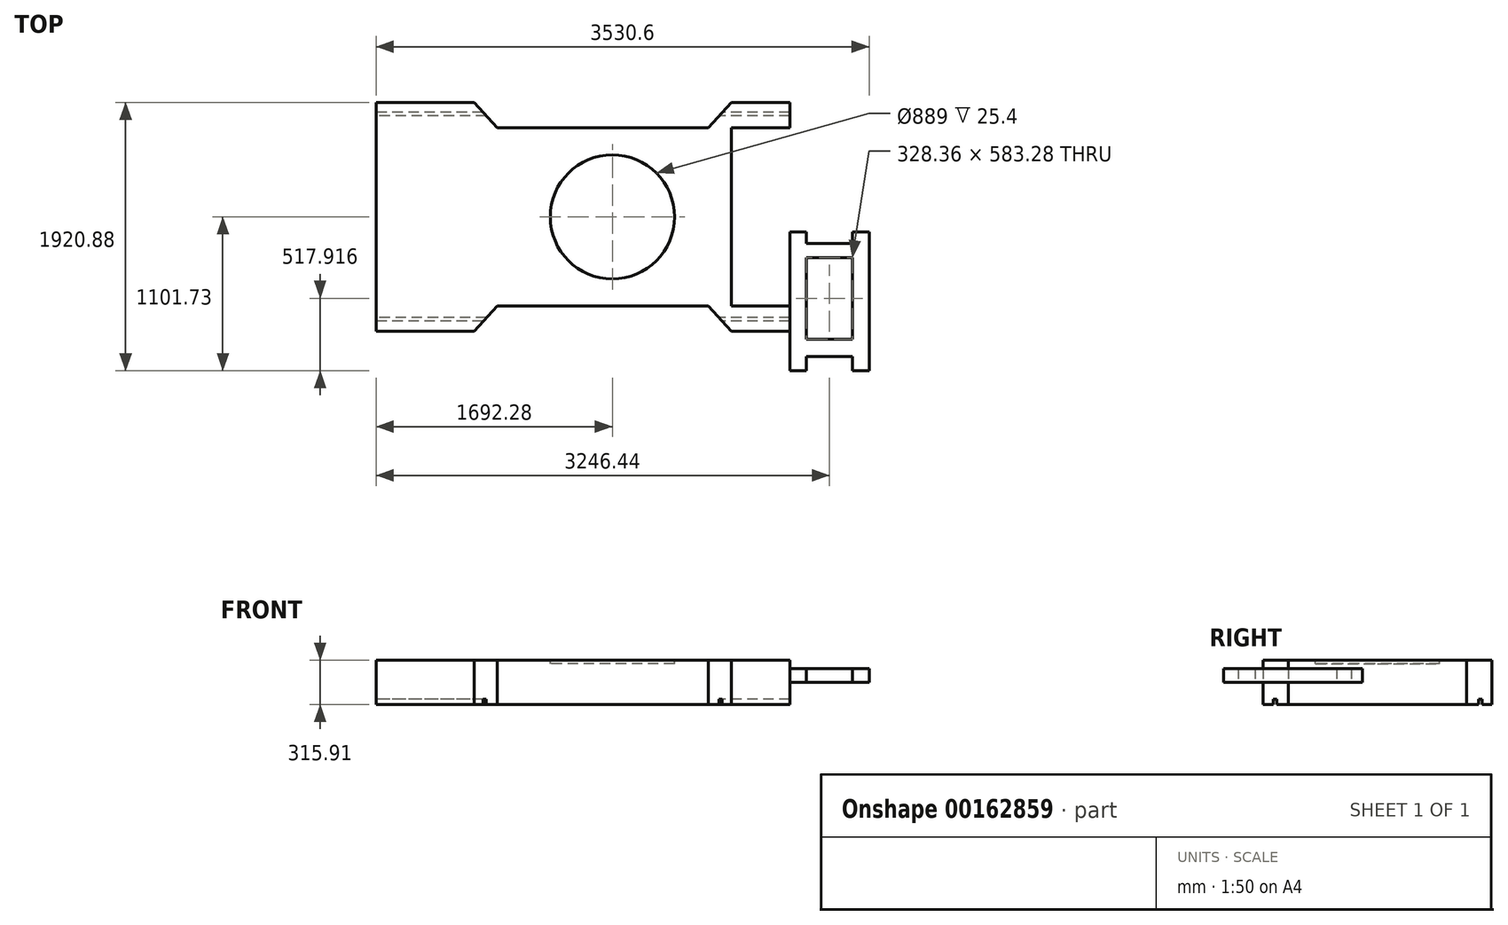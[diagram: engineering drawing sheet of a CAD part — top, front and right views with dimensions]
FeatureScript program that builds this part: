
annotation { "Feature Type Name" : "Feature", "Feature Type Description" : "" }
export const myFeature = defineFeature(function(context is Context, id is Id, definition is map)
    precondition{}
    {
        {
            var Q0;
            Q0=qCreatedBy(makeId("Top.planeOp"),FACE);
            var sketch = newSketch(context, id + "F0", { "sketchPlane" : qUnion([Q0])});
            skLineSegment(sketch, "E0.bottom", {"start": v(350.84, -819.15) * mm, "end": v(-350.84, -819.15) * mm});
            skLineSegment(sketch, "E0.top", {"start": v(350.84, 819.15) * mm, "end": v(-350.84, 819.15) * mm});
            skLineSegment(sketch, "E0.left", {"start": v(350.84, -819.15) * mm, "end": v(350.84, 819.15) * mm});
            skLineSegment(sketch, "E0.right", {"start": v(-350.84, -819.15) * mm, "end": v(-350.84, 819.15) * mm});
            skPoint(sketch, "E0.middle", {"position": v(0, 0) * mm});
            skLineSegment(sketch, "E1.bottom", {"start": v(350.84, -638.18) * mm, "end": v(2611.44, -638.17) * mm});
            skLineSegment(sketch, "E1.top", {"start": v(350.84, 638.17) * mm, "end": v(2611.44, 638.18) * mm});
            skPoint(sketch, "E1.middle", {"position": v(1538.92, 0) * mm});
            skPoint(sketch, "E1.left.end.orphan", {"position": v(-253.76, 638.17) * mm});
            skPoint(sketch, "E2.orphan", {"position": v(-253.76, -638.18) * mm});
            skLineSegment(sketch, "E3", {"start": v(350.84, -819.15) * mm, "end": v(515.94, -638.18) * mm});
            skLineSegment(sketch, "E4.MirrorCS", {"start": v(350.84, 819.15) * mm, "end": v(515.94, 638.18) * mm});
            skLineSegment(sketch, "E5", {"start": v(2027.24, 638.17) * mm, "end": v(2027.24, -638.17) * mm});
            skLineSegment(sketch, "E6", {"start": v(2192.34, 819.15) * mm, "end": v(2192.34, -732.4) * mm});
            skLineSegment(sketch, "E7", {"start": v(2192.34, -819.15) * mm, "end": v(2027.24, -638.17) * mm});
            skLineSegment(sketch, "E8", {"start": v(2192.34, -819.15) * mm, "end": v(2192.34, -732.4) * mm});
            skLineSegment(sketch, "E9", {"start": v(2027.24, 638.17) * mm, "end": v(2192.34, 819.15) * mm});
            skLineSegment(sketch, "E10", {"start": v(2611.44, 819.15) * mm, "end": v(2611.44, -1032) * mm});
            skLineSegment(sketch, "E11", {"start": v(2192.34, -819.15) * mm, "end": v(2611.44, -819.15) * mm});
            skLineSegment(sketch, "E12", {"start": v(2192.34, 819.15) * mm, "end": v(2611.44, 819.15) * mm});
            skPoint(sketch, "E13.orphan", {"position": v(3331.6, 638.18) * mm});
            skPoint(sketch, "E14.orphan", {"position": v(3331.6, -638.17) * mm});
            skLineSegment(sketch, "E15.bottom", {"start": v(2611.44, -107.95) * mm, "end": v(3179.76, -107.95) * mm});
            skLineSegment(sketch, "E15.top", {"start": v(2611.44, -1101.73) * mm, "end": v(3179.76, -1101.73) * mm});
            skLineSegment(sketch, "E15.left", {"start": v(2611.44, -107.95) * mm, "end": v(2611.44, -1101.73) * mm});
            skLineSegment(sketch, "E15.right", {"start": v(3179.76, -107.95) * mm, "end": v(3179.76, -1101.73) * mm});
            skLineSegment(sketch, "E16.bottom", {"start": v(3059.78, -875.45) * mm, "end": v(2731.42, -875.45) * mm});
            skLineSegment(sketch, "E16.top", {"start": v(3059.78, -292.18) * mm, "end": v(2731.42, -292.18) * mm});
            skLineSegment(sketch, "E16.left", {"start": v(3059.78, -875.45) * mm, "end": v(3059.78, -292.18) * mm});
            skLineSegment(sketch, "E16.right", {"start": v(2731.42, -875.45) * mm, "end": v(2731.42, -292.18) * mm});
            skPoint(sketch, "E16.middle", {"position": v(2895.6, -583.81) * mm});
            skPoint(sketch, "E16.middle.positionSnap0", {"position": v(2895.6, -1101.73) * mm});
            skPoint(sketch, "E16.centerSnap0", {"position": v(2895.6, -1101.73) * mm});
            skLineSegment(sketch, "E17.bottom", {"start": v(3059.78, -1204.11) * mm, "end": v(2731.42, -1204.11) * mm});
            skLineSegment(sketch, "E17.top", {"start": v(3059.78, -999.34) * mm, "end": v(2731.42, -999.34) * mm});
            skLineSegment(sketch, "E17.left", {"start": v(3059.78, -1204.11) * mm, "end": v(3059.78, -999.34) * mm});
            skLineSegment(sketch, "E17.right", {"start": v(2731.42, -1204.11) * mm, "end": v(2731.42, -999.34) * mm});
            skLineSegment(sketch, "E18.bottom", {"start": v(3059.78, -189.27) * mm, "end": v(2731.42, -189.27) * mm});
            skLineSegment(sketch, "E18.top", {"start": v(3059.78, -26.63) * mm, "end": v(2731.42, -26.63) * mm});
            skLineSegment(sketch, "E18.left", {"start": v(3059.78, -189.27) * mm, "end": v(3059.78, -26.63) * mm});
            skLineSegment(sketch, "E18.right", {"start": v(2731.42, -189.27) * mm, "end": v(2731.42, -26.63) * mm});
            skPoint(sketch, "E18.middle", {"position": v(2895.6, -107.95) * mm});
            skSolve(sketch);
        }
        {
            var Q0;
            {var subQ0=sQuery(id+"F0.wireOp",EDGE,"E4.MirrorCS");Q0=makeQuery(id+"F0.imprint","IMPRINT",FACE,{"disambiguationData":[TD([[makeQuery(id+"F0.imprint","IMPRINT",EDGE,{"derivedFrom":subQ0}),-1.0]])]});}
            var Q1;
            {var subQ0=sQuery(id+"F0.wireOp",EDGE,"E3");Q1=makeQuery(id+"F0.imprint","IMPRINT",FACE,{"disambiguationData":[TD([[makeQuery(id+"F0.imprint","IMPRINT",EDGE,{"derivedFrom":subQ0}),1.0]])]});}
            var Q2;
            {var subQ7=sQuery(id+"F0.wireOp",EDGE,"E5");Q2=makeQuery(id+"F0.imprint","IMPRINT",FACE,{"disambiguationData":[TD([[makeQuery(id+"F0.imprint","IMPRINT",EDGE,{"derivedFrom":subQ7}),-1.0]])]});}
            var Q3;
            {var subQ0=sQuery(id+"F0.wireOp",EDGE,"E5");Q3=makeQuery(id+"F0.imprint","IMPRINT",FACE,{"disambiguationData":[TD([[makeQuery(id+"F0.imprint","IMPRINT",EDGE,{"derivedFrom":subQ0}),1.0]])]});}
            var Q4;
            {var subQ5=sQuery(id+"F0.wireOp",EDGE,"E12");Q4=makeQuery(id+"F0.imprint","IMPRINT",FACE,{"disambiguationData":[TD([[makeQuery(id+"F0.imprint","IMPRINT",EDGE,{"derivedFrom":subQ5}),-1.0]])]});}
            var Q5;
            {var subQ1=sQuery(id+"F0.wireOp",EDGE,"E1.bottom");var subQ7=sQuery(id+"F0.wireOp",EDGE,"E15.left");var subQ9=makeQuery(id+"F0.imprint","INTERSECT",VERTEX,{"derivedFrom":[subQ1,subQ7]});Q5=makeQuery(id+"F0.imprint","IMPRINT",FACE,{"disambiguationData":[TD([[makeQuery(id+"F0.imprint","IMPRINT",EDGE,{"disambiguationData":[TD([[subQ9,1.0]])],"derivedFrom":subQ1}),1.0]])]});}
            var Q6;
            {var subQ0=sQuery(id+"F0.wireOp",EDGE,"E8");Q6=makeQuery(id+"F0.imprint","IMPRINT",FACE,{"disambiguationData":[TD([[makeQuery(id+"F0.imprint","IMPRINT",EDGE,{"derivedFrom":subQ0}),-1.0]])]});}
            var Q7;
            {var subQ0=sQuery(id+"F0.wireOp",EDGE,"E7");Q7=makeQuery(id+"F0.imprint","IMPRINT",FACE,{"disambiguationData":[TD([[makeQuery(id+"F0.imprint","IMPRINT",EDGE,{"derivedFrom":subQ0}),-1.0]])]});}
            var Q8;
            {var subQ3=sQuery(id+"F0.wireOp",EDGE,"E0.bottom");Q8=makeQuery(id+"F0.imprint","IMPRINT",FACE,{"disambiguationData":[TD([[makeQuery(id+"F0.imprint","IMPRINT",EDGE,{"derivedFrom":subQ3}),-1.0]])]});}
            var Q9;
            {var subQ0=sQuery(id+"F0.wireOp",EDGE,"E9");Q9=makeQuery(id+"F0.imprint","IMPRINT",FACE,{"disambiguationData":[TD([[makeQuery(id+"F0.imprint","IMPRINT",EDGE,{"derivedFrom":subQ0}),-1.0]])]});}
            var Q10;
            {var subQ5=sQuery(id+"F0.wireOp",EDGE,"E15.right");Q10=makeQuery(id+"F0.imprint","IMPRINT",FACE,{"disambiguationData":[TD([[makeQuery(id+"F0.imprint","IMPRINT",EDGE,{"derivedFrom":subQ5}),-1.0]])]});}
            extrude(context, id + "F1", {"entities" : qUnion([Q0, Q1, Q2, Q3, Q4, Q5, Q6, Q7, Q8, Q9, Q10]), "depth" : 315.91 * mm});
        }
        {
            var Q0;
            {var subQ5=sQuery(id+"F0.wireOp",EDGE,"E15.right");Q0=makeQuery(id+"F0.imprint","IMPRINT",FACE,{"disambiguationData":[TD([[makeQuery(id+"F0.imprint","IMPRINT",EDGE,{"derivedFrom":subQ5}),-1.0]])]});}
            cPlane(context, id + "F2", {"entities" : qUnion([Q0]), "cplaneType" : CPlaneType.OFFSET, "offset" : 101.6 * mm, "width" : 152.4 * mm, "height" : 152.4 * mm});
        }
        {
            var Q0;
            Q0=makeQuery(id+"F1.opExtrude","SWEPT_FACE",FACE,{"disambiguationData":[OSD([sQuery(id+"F0.wireOp",EDGE,"E15.right")])]});
            var sketch = newSketch(context, id + "F3", { "sketchPlane" : qUnion([Q0])});
            skLineSegment(sketch, "E19.bottom", {"start": v(-1101.73, 315.91) * mm, "end": v(-107.95, 315.91) * mm});
            skLineSegment(sketch, "E19.top", {"start": v(-1101.73, 258.28) * mm, "end": v(-107.95, 258.28) * mm});
            skLineSegment(sketch, "E19.left", {"start": v(-1101.73, 315.91) * mm, "end": v(-1101.73, 258.28) * mm});
            skLineSegment(sketch, "E19.right", {"start": v(-107.95, 315.91) * mm, "end": v(-107.95, 258.28) * mm});
            skLineSegment(sketch, "E20.bottom", {"start": v(-1101.73, 0) * mm, "end": v(-107.95, 0) * mm});
            skLineSegment(sketch, "E20.top", {"start": v(-1101.73, 157.96) * mm, "end": v(-107.95, 157.96) * mm});
            skLineSegment(sketch, "E20.left", {"start": v(-1101.73, 0) * mm, "end": v(-1101.73, 157.96) * mm});
            skLineSegment(sketch, "E20.right", {"start": v(-107.95, 0) * mm, "end": v(-107.95, 157.96) * mm});
            skSolve(sketch);
        }
        {
            var Q0;
            Q0 = qSketchRegion(id + "F3", true);
            extrude(context, id + "F4", {"entities" : qUnion([Q0]), "operationType" : NewBodyOperationType.REMOVE, "oppositeDirection" : true, "depth" : 568.32 * mm});
        }
        {
            var Q0;
            Q0=makeQuery(id+"F1.opExtrude","CAP_FACE",FACE,{"disambiguationData":[OSD([sQuery(id+"F0.wireOp",EDGE,"E0.bottom"),sQuery(id+"F0.wireOp",EDGE,"E0.top"),sQuery(id+"F0.wireOp",EDGE,"E0.right"),sQuery(id+"F0.wireOp",EDGE,"E1.bottom"),sQuery(id+"F0.wireOp",EDGE,"E1.top"),sQuery(id+"F0.wireOp",EDGE,"E3"),sQuery(id+"F0.wireOp",EDGE,"E4.MirrorCS"),sQuery(id+"F0.wireOp",EDGE,"E7"),sQuery(id+"F0.wireOp",EDGE,"E9"),sQuery(id+"F0.wireOp",EDGE,"E10"),sQuery(id+"F0.wireOp",EDGE,"E11"),sQuery(id+"F0.wireOp",EDGE,"E12"),sQuery(id+"F0.wireOp",EDGE,"E15.bottom"),sQuery(id+"F0.wireOp",EDGE,"E15.top"),sQuery(id+"F0.wireOp",EDGE,"E15.left"),sQuery(id+"F0.wireOp",EDGE,"E15.right"),sQuery(id+"F0.wireOp",EDGE,"E16.bottom"),sQuery(id+"F0.wireOp",EDGE,"E16.top"),sQuery(id+"F0.wireOp",EDGE,"E16.left"),sQuery(id+"F0.wireOp",EDGE,"E16.right"),sQuery(id+"F0.wireOp",EDGE,"E17.top"),sQuery(id+"F0.wireOp",EDGE,"E17.left"),sQuery(id+"F0.wireOp",EDGE,"E17.right"),sQuery(id+"F0.wireOp",EDGE,"E18.bottom"),sQuery(id+"F0.wireOp",EDGE,"E18.left"),sQuery(id+"F0.wireOp",EDGE,"E18.right")])],"isStart":false});
            var sketch = newSketch(context, id + "F5", { "sketchPlane" : qUnion([Q0])});
            skCircle(sketch, "E21", {"center": v(1341.44, 0) * mm, "radius": 444.5 * mm});
            skPoint(sketch, "E21.centerSnap0", {"position": v(2611.44, 0) * mm});
            skSolve(sketch);
        }
        {
            var Q0;
            Q0=makeQuery(id+"F5.imprint","IMPRINT",FACE,{"disambiguationData":[TD([[makeQuery(id+"F5.imprint","IMPRINT",EDGE,{"derivedFrom":sQuery(id+"F5.wireOp",EDGE,"E21")}),1.0]])]});
            extrude(context, id + "F6", {"entities" : qUnion([Q0]), "operationType" : NewBodyOperationType.REMOVE, "oppositeDirection" : true, "depth" : 25.4 * mm});
        }
        {
            var Q0;
            Q0=makeQuery(id+"F1.opExtrude","SWEPT_FACE",FACE,{"disambiguationData":[OSD([sQuery(id+"F0.wireOp",EDGE,"E0.right")])]});
            var sketch = newSketch(context, id + "F7", { "sketchPlane" : qUnion([Q0])});
            skLineSegment(sketch, "E22.bottom", {"start": v(-722.31, -38.1) * mm, "end": v(-747.71, -38.1) * mm});
            skLineSegment(sketch, "E22.top", {"start": v(-722.31, 38.1) * mm, "end": v(-747.71, 38.1) * mm});
            skLineSegment(sketch, "E22.left", {"start": v(-722.31, -38.1) * mm, "end": v(-722.31, 38.1) * mm});
            skLineSegment(sketch, "E22.right", {"start": v(-747.71, -38.1) * mm, "end": v(-747.71, 38.1) * mm});
            skPoint(sketch, "E22.middle", {"position": v(-735.01, 0) * mm});
            skLineSegment(sketch, "E23.MirrorCS", {"start": v(722.31, -38.1) * mm, "end": v(722.31, 38.1) * mm});
            skLineSegment(sketch, "E24.MirrorCS", {"start": v(722.31, 38.1) * mm, "end": v(747.71, 38.1) * mm});
            skLineSegment(sketch, "E25.MirrorCS", {"start": v(722.31, -38.1) * mm, "end": v(747.71, -38.1) * mm});
            skPoint(sketch, "E26.MirrorP", {"position": v(735.01, 0) * mm});
            skLineSegment(sketch, "E27.MirrorCS", {"start": v(747.71, -38.1) * mm, "end": v(747.71, 38.1) * mm});
            skSolve(sketch);
        }
        {
            var Q0;
            {var subQ0=sQuery(id+"F7.wireOp",EDGE,"E22.top");Q0=makeQuery(id+"F7.imprint","IMPRINT",FACE,{"disambiguationData":[TD([[makeQuery(id+"F7.imprint","IMPRINT",EDGE,{"derivedFrom":subQ0}),1.0]])]});}
            var Q1;
            {var subQ0=sQuery(id+"F7.wireOp",EDGE,"E24.MirrorCS");Q1=makeQuery(id+"F7.imprint","IMPRINT",FACE,{"disambiguationData":[TD([[makeQuery(id+"F7.imprint","IMPRINT",EDGE,{"derivedFrom":subQ0}),-1.0]])]});}
            extrude(context, id + "F8", {"entities" : qUnion([Q0, Q1]), "operationType" : NewBodyOperationType.REMOVE, "endBound" : BoundingType.THROUGH_ALL, "oppositeDirection" : true, "depth" : 25.4 * mm});
        }
    });
